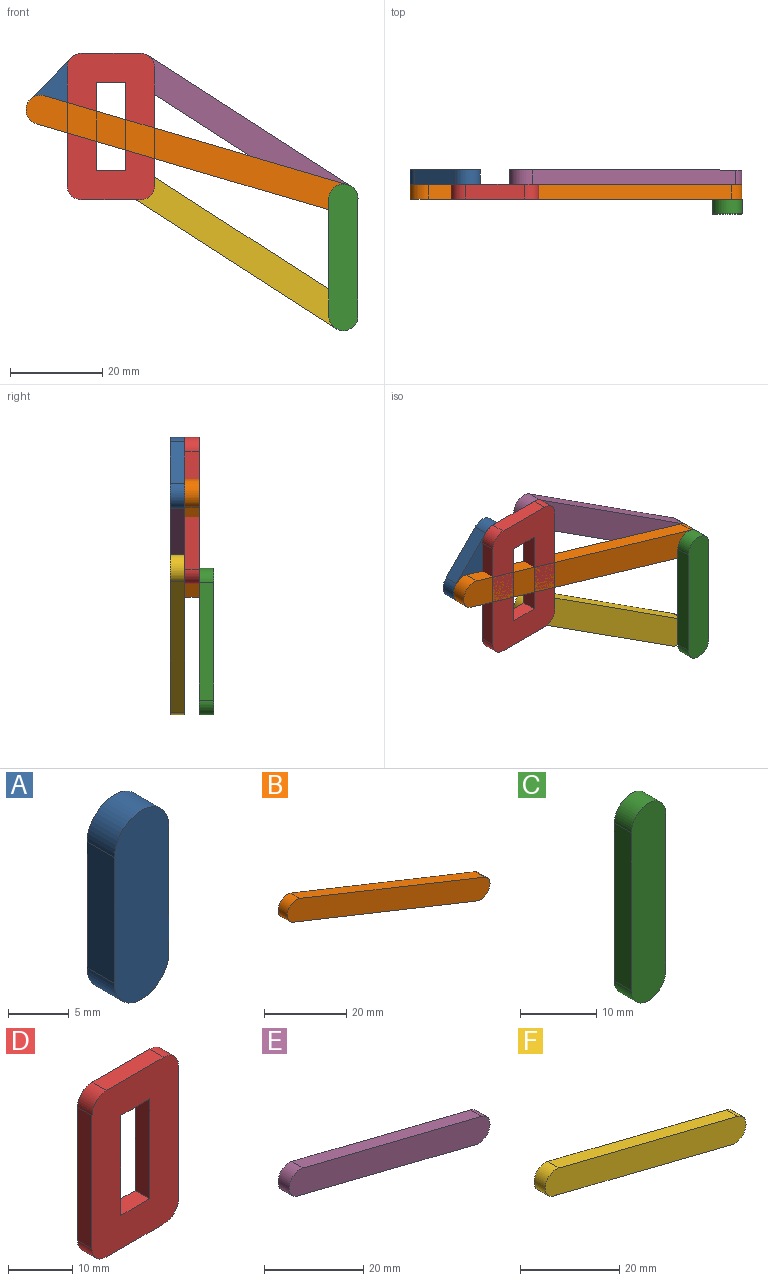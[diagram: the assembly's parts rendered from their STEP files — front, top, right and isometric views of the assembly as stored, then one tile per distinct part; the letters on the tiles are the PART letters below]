
ASSEMBLY  parts=6 mates=7
PART A: 6 faces, bbox 6.4x3.2x19.1 mm
  f0: plane 12.7x3.18mm, normal (1,0,0), area 40.3mm2, adj f1,f3,f4,f5
  f1: cylinder r=3.17mm len=6.35mm, axis (0,-1,0), area 31.7mm2, adj f0,f2,f4,f5
  f2: plane 12.7x3.18mm, normal (-1,0,0), area 40.3mm2, adj f1,f3,f4,f5
  f3: cylinder r=3.17mm len=6.35mm, axis (0,-1,0), area 31.7mm2, adj f0,f2,f4,f5
  f4: plane 19.05x6.35mm, normal (0,1,0), area 112.3mm2, adj f0,f1,f2,f3
  f5: plane 19.05x6.35mm, normal (0,-1,0), area 112.3mm2, adj f0,f1,f2,f3
PART B: 6 faces, bbox 69.9x3.2x31.8 mm
  f0: cylinder r=3.17mm len=6.12mm, axis (0,1,0), area 31.7mm2, adj f1,f3,f4,f5
  f1: plane 63.5x25.4mm, normal (-0.37,0,-0.93), area 217.1mm2, adj f0,f2,f4,f5
  f2: cylinder r=3.17mm len=6.12mm, axis (0,1,0), area 31.7mm2, adj f1,f3,f4,f5
  f3: plane 63.5x25.4mm, normal (0.37,0,0.93), area 217.1mm2, adj f0,f2,f4,f5
  f4: plane 69.85x31.75mm, normal (0,-1,0), area 466mm2, adj f0,f1,f2,f3
  f5: plane 69.85x31.75mm, normal (0,1,0), area 466mm2, adj f0,f1,f2,f3
PART C: 6 faces, bbox 6.4x3.2x31.8 mm
  f0: plane 25.4x3.18mm, normal (1,0,0), area 80.6mm2, adj f1,f3,f4,f5
  f1: cylinder r=3.17mm len=6.35mm, axis (0,1,0), area 31.7mm2, adj f0,f2,f4,f5
  f2: plane 25.4x3.18mm, normal (-1,0,0), area 80.6mm2, adj f1,f3,f4,f5
  f3: cylinder r=3.17mm len=6.35mm, axis (0,1,0), area 31.7mm2, adj f0,f2,f4,f5
  f4: plane 31.75x6.35mm, normal (0,-1,0), area 193mm2, adj f0,f1,f2,f3
  f5: plane 31.75x6.35mm, normal (0,1,0), area 193mm2, adj f0,f1,f2,f3
PART D: 15 faces, bbox 19.1x3.2x31.8 mm
  f0: plane 19.05x3.18mm, normal (1,0,0), area 60.5mm2, adj f1,f12,f13,f14
  f1: plane 6.35x3.18mm, normal (0,0,-1), area 20.2mm2, adj f0,f2,f13,f14
  f2: plane 19.05x3.18mm, normal (-1,0,0), area 60.5mm2, adj f1,f12,f13,f14
  f3: plane 12.7x3.18mm, normal (0,0,1), area 40.3mm2, adj f4,f11,f13,f14
  f4: cylinder r=3.17mm len=3.18mm, axis (0,1,0), area 15.8mm2, adj f3,f5,f13,f14
  f5: plane 25.4x3.18mm, normal (-1,0,0), area 80.6mm2, adj f4,f6,f13,f14
  f6: cylinder r=3.17mm len=3.18mm, axis (0,1,0), area 15.8mm2, adj f5,f7,f13,f14
  f7: plane 12.31x3.18mm, normal (0,0,-1), area 39.1mm2, adj f6,f8,f13,f14
  f8: plane 3.18x0.38mm, normal (0.24,0,0.97), area 1.2mm2, adj f7,f9,f13,f14
  f9: cylinder r=3.17mm len=3.95mm, axis (0,1,0), area 18.3mm2, adj f8,f10,f13,f14
  f10: plane 25.4x3.18mm, normal (1,0,0), area 80.6mm2, adj f9,f11,f13,f14
  f11: cylinder r=3.17mm len=3.18mm, axis (0,1,0), area 15.8mm2, adj f3,f10,f13,f14
  f12: plane 6.35x3.18mm, normal (0,0,1), area 20.2mm2, adj f0,f2,f13,f14
  f13: plane 31.75x19.05mm, normal (0,-1,0), area 475.2mm2, adj f0,f1,f2,f3,f4,f5,f6,f7
  f14: plane 31.75x19.05mm, normal (0,1,0), area 475.2mm2, adj f0,f1,f2,f3,f4,f5,f6,f7
PART E: 6 faces, bbox 57.2x3.2x19.1 mm
  f0: plane 50.8x12.7mm, normal (-0.24,0,-0.97), area 166.3mm2, adj f1,f3,f4,f5
  f1: cylinder r=3.17mm len=6.26mm, axis (0,-1,0), area 31.7mm2, adj f0,f2,f4,f5
  f2: plane 50.8x12.7mm, normal (0.24,0,0.97), area 166.3mm2, adj f1,f3,f4,f5
  f3: cylinder r=3.17mm len=6.26mm, axis (0,-1,0), area 31.7mm2, adj f0,f2,f4,f5
  f4: plane 57.15x19.05mm, normal (0,1,0), area 364.2mm2, adj f0,f1,f2,f3
  f5: plane 57.15x19.05mm, normal (0,-1,0), area 364.2mm2, adj f0,f1,f2,f3
PART F: 7 faces, bbox 57.2x3.2x19.1 mm
  f0: cylinder r=3.17mm len=6.35mm, axis (0,-1,0), area 34.1mm2, adj f1,f4,f5,f6
  f1: plane 3.18x0.39mm, normal (0,0,1), area 1.2mm2, adj f0,f2,f5,f6
  f2: plane 50.42x12.61mm, normal (-0.24,0,-0.97), area 165mm2, adj f1,f3,f5,f6
  f3: cylinder r=3.17mm len=6.26mm, axis (0,-1,0), area 31.7mm2, adj f2,f4,f5,f6
  f4: plane 50.8x12.7mm, normal (0.24,0,0.97), area 166.3mm2, adj f0,f3,f5,f6
  f5: plane 57.15x19.05mm, normal (0,1,0), area 364.2mm2, adj f0,f1,f2,f3,f4
  f6: plane 57.15x19.05mm, normal (0,-1,0), area 364.2mm2, adj f0,f1,f2,f3,f4
PLACE A rot(axis=(0.93,0,-0.38),180deg) t=(26.86,4.76,37.81)mm
PLACE B rot(axis=(0.94,0,-0.33),180deg) t=(24.64,-1.59,41.6)mm
PLACE C rot(axis=(0,0,-1),180deg) t=(107.52,-4.76,-12.49)mm
PLACE D t=(12.7,1.59,3.17)mm
PLACE E rot(axis=(0,1,0),18.8deg) t=(4.53,1.59,4.52)mm
PLACE F rot(axis=(-0.92,0,0.4),180deg) t=(12.7,4.76,3.17)mm
MATE revolute F.f0 <-> D.f9  axis (0,-1,0) through (12.7,1.59,3.17)mm
MATE revolute A.f3 <-> D.f4  axis (0,-1,0) through (0,1.59,28.58)mm
MATE revolute E.f1 <-> C.f1  axis (0,-1,0) through (56.72,1.59,0.21)mm
MATE revolute E.f3 <-> D.f11  axis (0,-1,0) through (12.7,1.59,28.58)mm
MATE revolute B.f2 <-> C.f1  axis (0,-1,0) through (56.72,-1.59,0.21)mm
MATE revolute C.f3 <-> F.f3  axis (0,1,0) through (56.72,-1.59,-25.19)mm
MATE revolute B.f0 <-> A.f1  axis (0,1,0) through (-8.9,1.59,19.51)mm
